# Revit family: Beam One
name_source: partatom
category: Lighting Fixtures
revit_build: Autodesk Revit 2018 (Build: 20170223_1515(x64)
units: mm (PartAtom-declared; Revit-internal decimal feet)

## family parameters
Always vertical = Yes
Cut with Voids When Loaded = No
Light Source = Yes
OmniClass Number = 23.80.70.00
OmniClass Title = Lighting
Part Type = Normal
Room Calculation Point = No
Round Connector Dimension = Use Diameter
Shared = No
Work Plane-Based = No

## types (1)
- CE
    Color Filter = 16777215
    Dimmable = Yes
    Dimming Lamp Color Temperature Shift = <None>
    Dimming Method = Driver Dependent
    Driver Included = No
    Driver Required = Yes
    Efficacy (lm/W) = Driver Dependent
    Electrical Class = Class III
    Lamp = Dedicated LED
    Length of Cable Supplied = 1m
    Light Source Fixed = Yes
    Location Rating = IP65
    Main Finish = Painted Silver
    Main Material = Aluminium
    Photometric Web File = IESN_0937-3000K-Q5.IES
    Power (W) = 2.2W
    Prdouct Code = 0937
    Product Location = Outdoor
    Product Name = Beam One
    Product SKU = 1202001
    Tilt Angle = 90.00°
    Wattage Comments = Driver Dependent

## geometry (parser evidence)
native form markers: Sweep x3
no freeform markers — native parametric forms only
